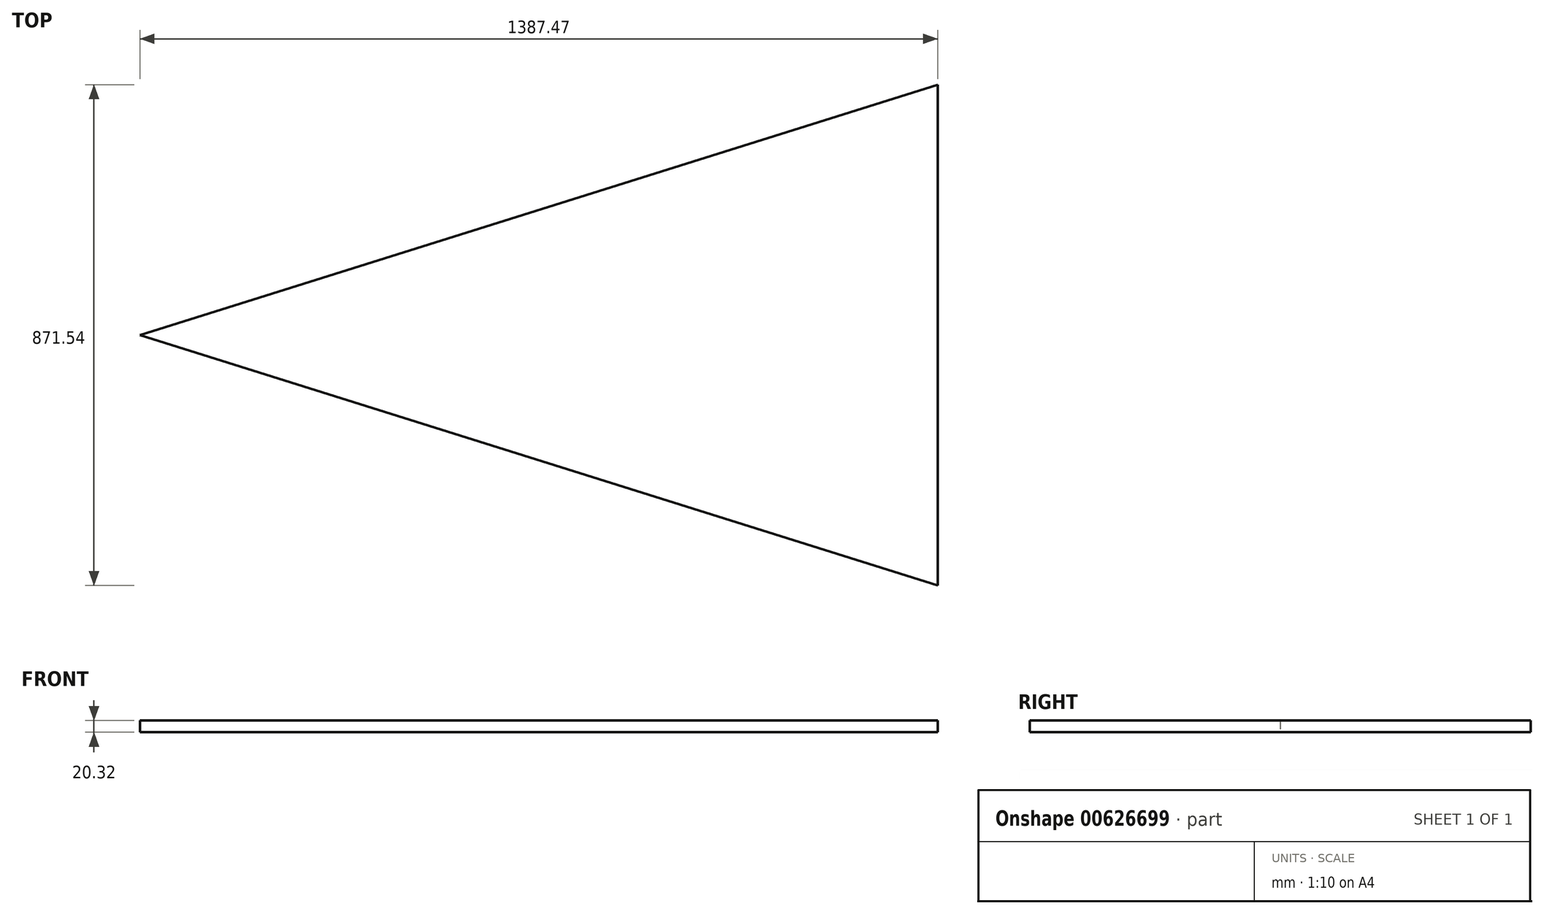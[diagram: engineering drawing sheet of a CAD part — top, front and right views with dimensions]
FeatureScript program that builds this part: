
annotation { "Feature Type Name" : "Feature", "Feature Type Description" : "" }
export const myFeature = defineFeature(function(context is Context, id is Id, definition is map)
    precondition{}
    {
        {
            var Q0;
            Q0=qCreatedBy(makeId("Top.planeOp"),FACE);
            var sketch = newSketch(context, id + "F0", { "sketchPlane" : qUnion([Q0])});
            skLineSegment(sketch, "E0", {"start": v(0, 0) * mm, "end": v(1387.48, -435.77) * mm});
            skLineSegment(sketch, "E1", {"start": v(1387.47, -435.77) * mm, "end": v(1387.47, 435.77) * mm});
            skLineSegment(sketch, "E2", {"start": v(-193.2, 0) * mm, "end": v(1688.97, 0) * mm, "construction": true});
            skLineSegment(sketch, "E3.MirrorCS", {"start": v(0, 0) * mm, "end": v(1387.48, 435.77) * mm});
            skSolve(sketch);
        }
        {
            var Q0;
            Q0 = qSketchRegion(id + "F0", true);
            extrude(context, id + "F1", {"entities" : qUnion([Q0]), "depth" : 20.32 * mm, "offsetDistance" : 25.4 * mm});
        }
    });
